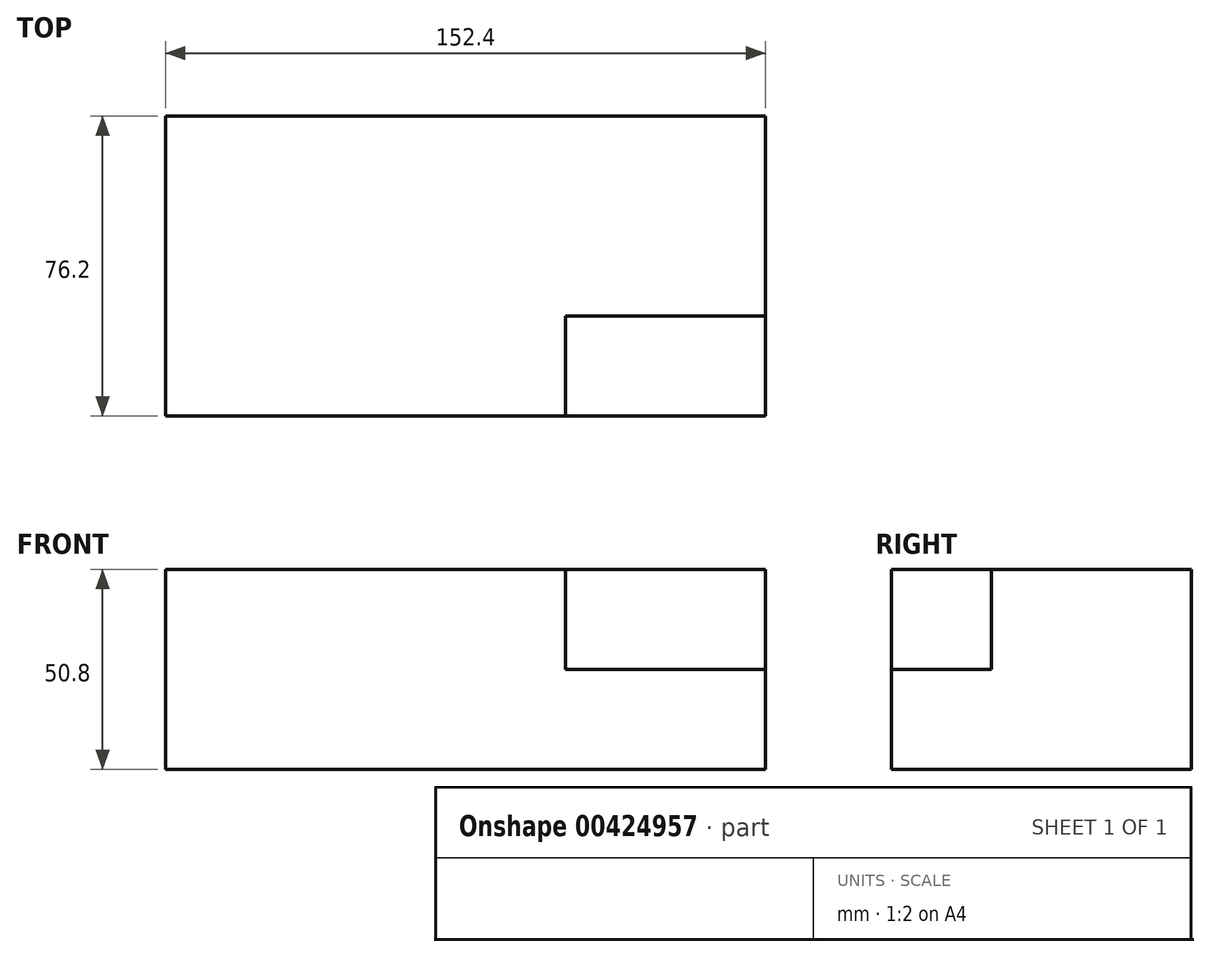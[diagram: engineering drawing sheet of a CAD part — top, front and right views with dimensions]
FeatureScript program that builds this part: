
annotation { "Feature Type Name" : "Feature", "Feature Type Description" : "" }
export const myFeature = defineFeature(function(context is Context, id is Id, definition is map)
    precondition{}
    {
        {
            var Q0;
            Q0=qCreatedBy(makeId("Top.planeOp"),FACE);
            var sketch = newSketch(context, id + "F0", { "sketchPlane" : qUnion([Q0])});
            skLineSegment(sketch, "E0", {"start": v(0, 0) * mm, "end": v(152.4, 0) * mm});
            skLineSegment(sketch, "E1", {"start": v(152.4, 0) * mm, "end": v(152.4, 76.2) * mm});
            skLineSegment(sketch, "E2", {"start": v(152.4, 76.2) * mm, "end": v(0, 76.2) * mm});
            skLineSegment(sketch, "E3", {"start": v(0, 76.2) * mm, "end": v(0, 0) * mm});
            skSolve(sketch);
        }
        {
            var Q0;
            Q0=makeQuery(id+"F0.imprint","IMPRINT",FACE,{"disambiguationData":[TD([[makeQuery(id+"F0.imprint","IMPRINT",EDGE,{"derivedFrom":sQuery(id+"F0.wireOp",EDGE,"E0")}),1.0]])]});
            extrude(context, id + "F1", {"entities" : qUnion([Q0]), "depth" : 50.8 * mm});
        }
        {
            var Q0;
            Q0=makeQuery(id+"F1.opExtrude","SWEPT_FACE",FACE,{"disambiguationData":[OSD([sQuery(id+"F0.wireOp",EDGE,"E0")])]});
            var sketch = newSketch(context, id + "F2", { "sketchPlane" : qUnion([Q0])});
            skLineSegment(sketch, "E4", {"start": v(152.4, 50.8) * mm, "end": v(101.6, 50.8) * mm});
            skLineSegment(sketch, "E5", {"start": v(101.6, 50.8) * mm, "end": v(101.6, 25.4) * mm});
            skLineSegment(sketch, "E6", {"start": v(101.6, 25.4) * mm, "end": v(152.4, 25.4) * mm});
            skLineSegment(sketch, "E7", {"start": v(152.4, 25.4) * mm, "end": v(152.4, 48.23) * mm});
            skSolve(sketch);
        }
        {
            var Q0;
            {var subQ1=sQuery(id+"F2.wireOp",EDGE,"E4");Q0=makeQuery(id+"F2.imprint","IMPRINT",FACE,{"disambiguationData":[TD([[makeQuery(id+"F2.imprint","IMPRINT",EDGE,{"derivedFrom":subQ1}),-1.0]])]});}
            extrude(context, id + "F3", {"entities" : qUnion([Q0]), "operationType" : NewBodyOperationType.REMOVE, "oppositeDirection" : true, "depth" : 25.4 * mm});
        }
    });
